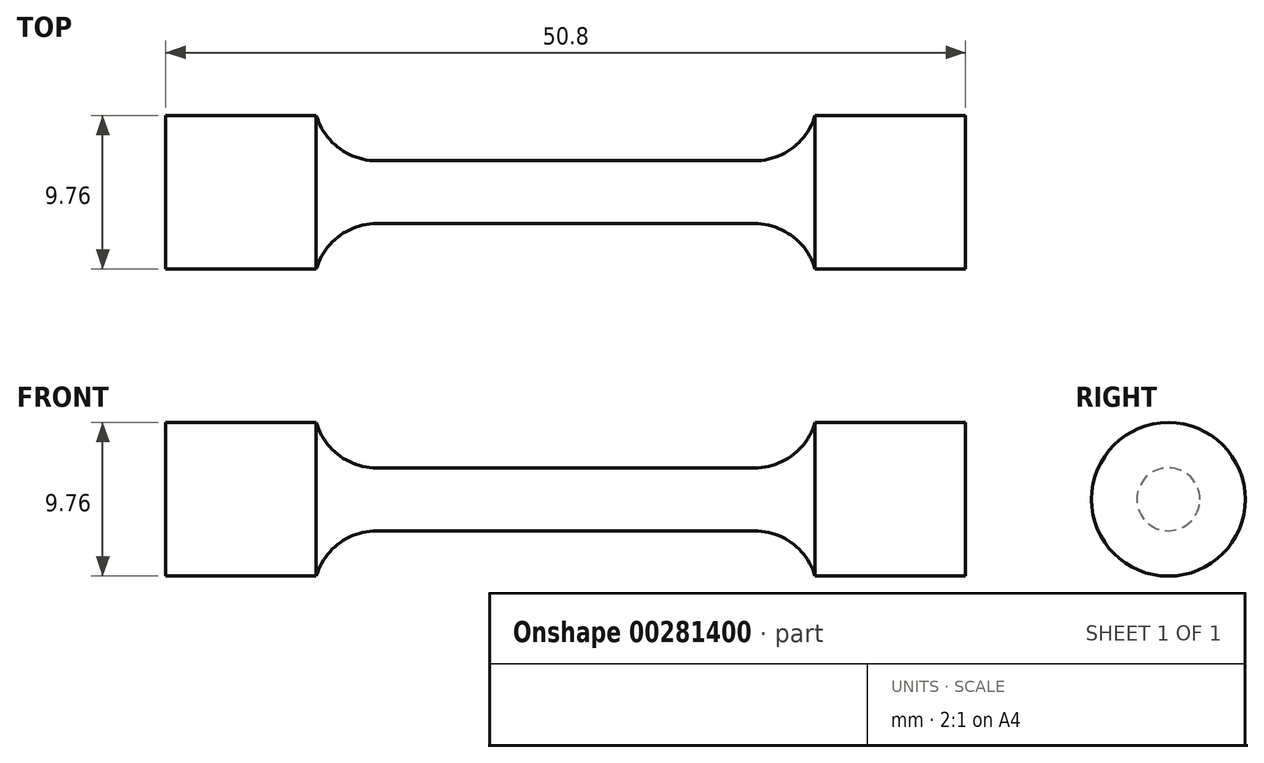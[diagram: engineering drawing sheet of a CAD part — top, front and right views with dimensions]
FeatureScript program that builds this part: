
annotation { "Feature Type Name" : "Feature", "Feature Type Description" : "" }
export const myFeature = defineFeature(function(context is Context, id is Id, definition is map)
    precondition{}
    {
        {
            var Q0;
            Q0=qCreatedBy(makeId("Front.planeOp"),FACE);
            var sketch = newSketch(context, id + "F0", { "sketchPlane" : qUnion([Q0])});
            skLineSegment(sketch, "E0", {"start": v(0, 2) * mm, "end": v(12, 2) * mm});
            skArc(sketch, "E1", {"start": v(12, 2) * mm, "mid": v(14.4, 2.8) * mm, "end": v(15.84, 4.88) * mm});
            skLineSegment(sketch, "E2", {"start": v(15.84, 4.88) * mm, "end": v(25.4, 4.88) * mm});
            skLineSegment(sketch, "E3", {"start": v(25.4, 4.88) * mm, "end": v(25.4, 0) * mm});
            skLineSegment(sketch, "E4", {"start": v(0, 0) * mm, "end": v(25.4, 0) * mm});
            skLineSegment(sketch, "E5.MirrorCS", {"start": v(0, 2) * mm, "end": v(-12, 2) * mm});
            skLineSegment(sketch, "E6.MirrorCS", {"start": v(0, 0) * mm, "end": v(-25.4, 0) * mm});
            skLineSegment(sketch, "E7.MirrorCS", {"start": v(-15.84, 4.88) * mm, "end": v(-25.4, 4.88) * mm});
            skLineSegment(sketch, "E8.MirrorCS", {"start": v(-25.4, 4.88) * mm, "end": v(-25.4, 0) * mm});
            skArc(sketch, "E9.MirrorCS", {"start": v(-12, 2) * mm, "mid": v(-14.4, 2.8) * mm, "end": v(-15.84, 4.88) * mm});
            skSolve(sketch);
        }
        {
            var Q0;
            Q0=makeQuery(id+"F0.imprint","IMPRINT",FACE,{"disambiguationData":[TD([[makeQuery(id+"F0.imprint","IMPRINT",EDGE,{"derivedFrom":sQuery(id+"F0.wireOp",EDGE,"E0")}),-1.0]])]});
            var Q1;
            Q1=sQuery(id+"F0.wireOp",EDGE,"E9.MirrorCS");
            var Q2;
            Q2=sQuery(id+"F0.wireOp",EDGE,"E8.MirrorCS");
            var Q3;
            Q3=sQuery(id+"F0.wireOp",EDGE,"E7.MirrorCS");
            var Q4;
            Q4=sQuery(id+"F0.wireOp",EDGE,"E6.MirrorCS");
            var Q5;
            Q5=sQuery(id+"F0.wireOp",EDGE,"E0");
            var Q6;
            Q6=sQuery(id+"F0.wireOp",EDGE,"E1");
            var Q7;
            Q7=sQuery(id+"F0.wireOp",EDGE,"E2");
            var Q8;
            Q8=sQuery(id+"F0.wireOp",EDGE,"E3");
            var Q9;
            Q9=sQuery(id+"F0.wireOp",EDGE,"E4");
            var Q10;
            Q10=sQuery(id+"F0.wireOp",EDGE,"E5.MirrorCS");
            var Q11;
            Q11=sQuery(id+"F0.wireOp",EDGE,"E4");
            revolve(context, id + "F1", {"entities" : qUnion([Q0]), "surfaceEntities" : qUnion([Q1, Q2, Q3, Q4, Q5, Q6, Q7, Q8, Q9, Q10]), "axis" : qUnion([Q11]), "revolveType" : RevolveType.FULL});
        }
    });
